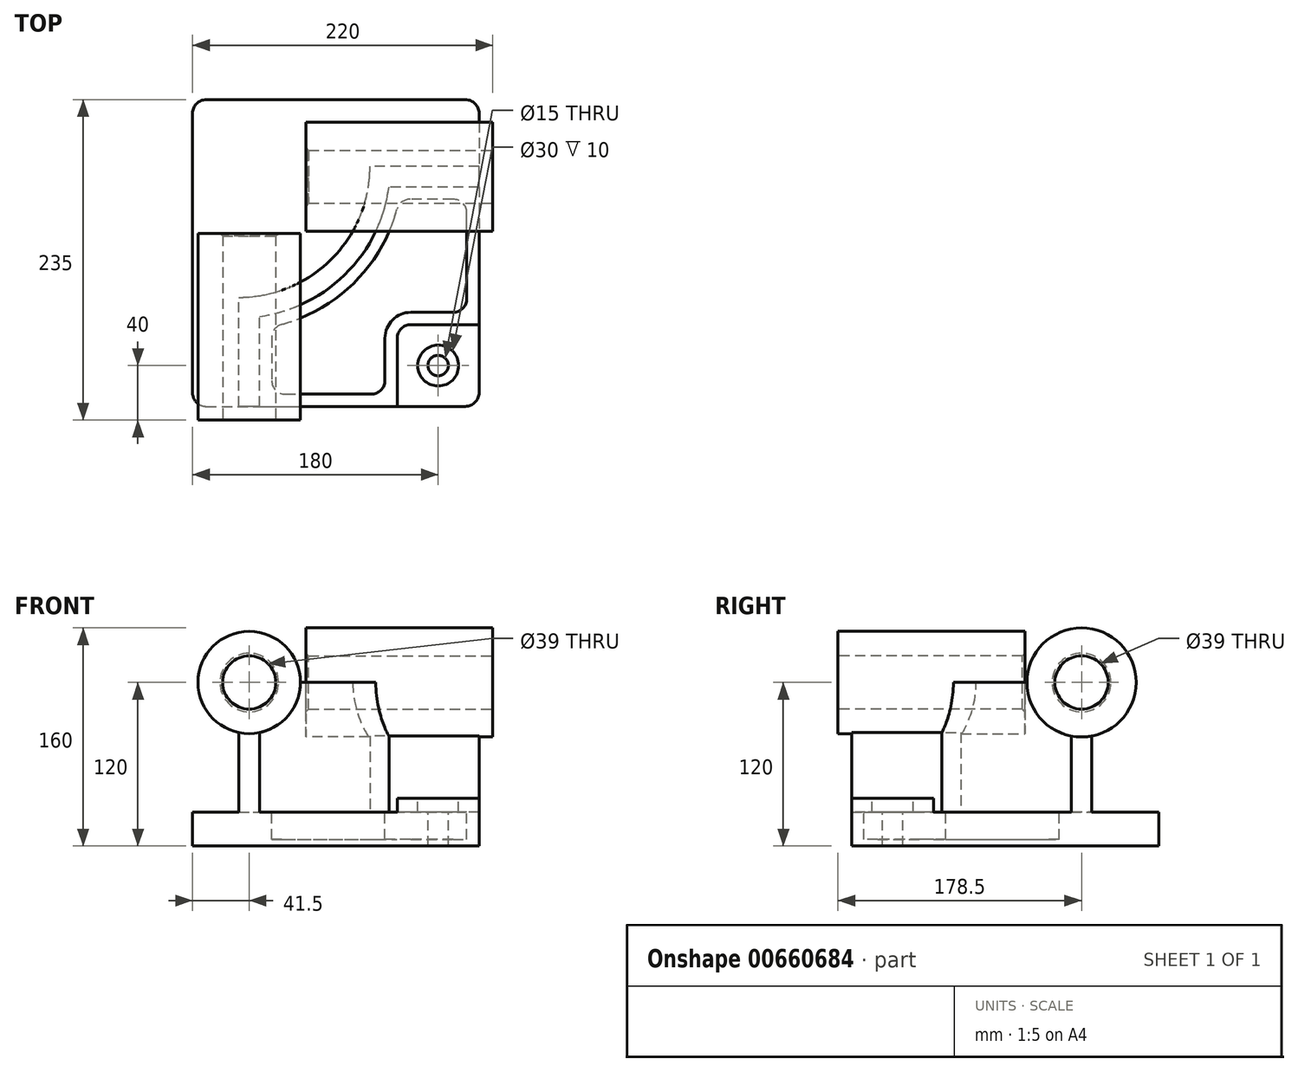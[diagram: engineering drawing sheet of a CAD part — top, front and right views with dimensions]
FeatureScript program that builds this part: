
annotation { "Feature Type Name" : "Feature", "Feature Type Description" : "" }
export const myFeature = defineFeature(function(context is Context, id is Id, definition is map)
    precondition{}
    {
        {
            var Q0;
            Q0=qCreatedBy(makeId("Top.planeOp"),FACE);
            var sketch = newSketch(context, id + "F0", { "sketchPlane" : qUnion([Q0])});
            skLineSegment(sketch, "E0.bottom", {"start": v(-105, 112.5) * mm, "end": v(105, 112.5) * mm});
            skLineSegment(sketch, "E0.top", {"start": v(-105, -112.5) * mm, "end": v(105, -112.5) * mm});
            skLineSegment(sketch, "E0.left", {"start": v(-105, 112.5) * mm, "end": v(-105, -112.5) * mm});
            skLineSegment(sketch, "E0.right", {"start": v(105, 112.5) * mm, "end": v(105, -112.5) * mm});
            skPoint(sketch, "E0.middle", {"position": v(0, 0) * mm});
            skSolve(sketch);
        }
        {
            var Q0;
            Q0=makeQuery(id+"F0.imprint","IMPRINT",FACE,{"disambiguationData":[TD([[makeQuery(id+"F0.imprint","IMPRINT",EDGE,{"derivedFrom":sQuery(id+"F0.wireOp",EDGE,"E0.bottom")}),-1.0]])]});
            extrude(context, id + "F1", {"entities" : qUnion([Q0]), "depth" : 25 * mm, "offsetDistance" : 25.4 * mm});
        }
        {
            var Q0;
            Q0=makeQuery(id+"F1.opExtrude","CAP_FACE",FACE,{"disambiguationData":[OSD([sQuery(id+"F0.wireOp",EDGE,"E0.bottom"),sQuery(id+"F0.wireOp",EDGE,"E0.top"),sQuery(id+"F0.wireOp",EDGE,"E0.left"),sQuery(id+"F0.wireOp",EDGE,"E0.right")])],"isStart":false});
            var sketch = newSketch(context, id + "F2", { "sketchPlane" : qUnion([Q0])});
            skLineSegment(sketch, "E1", {"start": v(-71, -112.5) * mm, "end": v(-71, -32.5) * mm});
            skLineSegment(sketch, "E2", {"start": v(105, 63.5) * mm, "end": v(25, 63.5) * mm});
            skArc(sketch, "E3", {"start": v(-71, -32.5) * mm, "mid": v(-3.12, -4.38) * mm, "end": v(25, 63.5) * mm});
            skLineSegment(sketch, "E4", {"start": v(-71, 63.5) * mm, "end": v(-71, -32.5) * mm, "construction": true});
            skLineSegment(sketch, "E5", {"start": v(-71, 63.5) * mm, "end": v(25, 63.5) * mm, "construction": true});
            skLineSegment(sketch, "E6.0", {"start": v(-56, -112.5) * mm, "end": v(-56, -46.48) * mm});
            skArc(sketch, "E6.1", {"start": v(-56, -46.48) * mm, "mid": v(7.49, -14.99) * mm, "end": v(38.98, 48.5) * mm});
            skLineSegment(sketch, "E6.2", {"start": v(105, 48.5) * mm, "end": v(38.98, 48.5) * mm});
            skLineSegment(sketch, "E7.0", {"start": v(-105, -112.5) * mm, "end": v(105, -112.5) * mm});
            skLineSegment(sketch, "E8.0", {"start": v(105, 112.5) * mm, "end": v(105, -112.5) * mm});
            skSolve(sketch);
        }
        {
            var Q0;
            {var subQ2=sQuery(id+"F2.wireOp",EDGE,"E1");Q0=makeQuery(id+"F2.imprint","IMPRINT",FACE,{"disambiguationData":[TD([[makeQuery(id+"F2.imprint","IMPRINT",EDGE,{"derivedFrom":subQ2}),-1.0]])]});}
            extrude(context, id + "F3", {"entities" : qUnion([Q0]), "operationType" : NewBodyOperationType.ADD, "depth" : 95 * mm, "offsetDistance" : 25.4 * mm});
        }
        {
            var Q0;
            Q0=makeQuery(id+"F3.boolean.opBoolean","MERGE",FACE,{"derivedFrom":[makeQuery(id+"F1.opExtrude","SWEPT_FACE",FACE,{"disambiguationData":[OSD([sQuery(id+"F0.wireOp",EDGE,"E0.top")])]}),makeQuery(id+"F3.opExtrude","SWEPT_FACE",FACE,{"disambiguationData":[OSD([sQuery(id+"F2.wireOp",EDGE,"E7.0")])]})]});
            var sketch = newSketch(context, id + "F4", { "sketchPlane" : qUnion([Q0])});
            skCircle(sketch, "E9", {"center": v(-63.5, 120) * mm, "radius": 37.5 * mm});
            skSolve(sketch);
        }
        {
            var Q0;
            Q0 = qSketchRegion(id + "F4", true);
            extrude(context, id + "F5", {"entities" : qUnion([Q0]), "operationType" : NewBodyOperationType.ADD, "depth" : 10 * mm, "offsetDistance" : 25.4 * mm, "hasSecondDirection" : true, "secondDirectionOppositeDirection" : true, "secondDirectionDepth" : (137 - 10) * mm});
        }
        {
            var Q0;
            Q0=makeQuery(id+"F3.boolean.opBoolean","MERGE",FACE,{"derivedFrom":[makeQuery(id+"F1.opExtrude","SWEPT_FACE",FACE,{"disambiguationData":[OSD([sQuery(id+"F0.wireOp",EDGE,"E0.right")])]}),makeQuery(id+"F3.opExtrude","SWEPT_FACE",FACE,{"disambiguationData":[OSD([sQuery(id+"F2.wireOp",EDGE,"E8.0")])]})]});
            var sketch = newSketch(context, id + "F6", { "sketchPlane" : qUnion([Q0])});
            skCircle(sketch, "E10", {"center": v(56, 120) * mm, "radius": 40 * mm});
            skSolve(sketch);
        }
        {
            var Q0;
            Q0 = qSketchRegion(id + "F6", true);
            extrude(context, id + "F7", {"entities" : qUnion([Q0]), "operationType" : NewBodyOperationType.ADD, "depth" : 10 * mm, "offsetDistance" : 25.4 * mm, "hasSecondDirection" : true, "secondDirectionOppositeDirection" : true, "secondDirectionDepth" : (137 - 10) * mm});
        }
        {
            var Q0;
            {var subQ0=sQuery(id+"F0.wireOp",EDGE,"E0.right");var subQ1=sQuery(id+"F0.wireOp",EDGE,"E0.top");Q0=makeQuery(id+"F3.boolean.opBoolean","SPLIT",FACE,{"disambiguationData":[TD([makeQuery(id+"F3.opExtrude","SWEPT_FACE",FACE,{"disambiguationData":[OSD([sQuery(id+"F2.wireOp",EDGE,"E6.0")])]})])],"derivedFrom":makeQuery(id+"F1.opExtrude","CAP_FACE",FACE,{"disambiguationData":[OSD([sQuery(id+"F0.wireOp",EDGE,"E0.bottom"),subQ1,sQuery(id+"F0.wireOp",EDGE,"E0.left"),subQ0])],"isStart":false})});}
            var sketch = newSketch(context, id + "F8", { "sketchPlane" : qUnion([Q0])});
            skLineSegment(sketch, "E11.bottom", {"start": v(105, -112.5) * mm, "end": v(45, -112.5) * mm});
            skLineSegment(sketch, "E11.top", {"start": v(105, -52.5) * mm, "end": v(45, -52.5) * mm});
            skLineSegment(sketch, "E11.left", {"start": v(105, -112.5) * mm, "end": v(105, -52.5) * mm});
            skLineSegment(sketch, "E11.right", {"start": v(45, -112.5) * mm, "end": v(45, -52.5) * mm});
            skSolve(sketch);
        }
        {
            var Q0;
            Q0 = qSketchRegion(id + "F8", true);
            extrude(context, id + "F9", {"entities" : qUnion([Q0]), "operationType" : NewBodyOperationType.ADD, "depth" : 10 * mm, "offsetDistance" : 25.4 * mm});
        }
        {
            var Q0;
            Q0=makeQuery(id+"F9.opExtrude","SWEPT_EDGE",EDGE,{"disambiguationData":[OSD([sQuery(id+"F8.wireOp",EDGE,"E11.top"),sQuery(id+"F8.wireOp",EDGE,"E11.right")])]});
            fillet(context, id + "F10", {"entities" : qUnion([Q0]), "radius" : 10 * mm, "tangentPropagation" : true, "allowEdgeOverflow" : false});
        }
        {
            var Q0;
            {var subQ0=sQuery(id+"F0.wireOp",EDGE,"E0.right");var subQ1=sQuery(id+"F0.wireOp",EDGE,"E0.top");Q0=makeQuery(id+"F3.boolean.opBoolean","SPLIT",FACE,{"disambiguationData":[TD([makeQuery(id+"F3.opExtrude","SWEPT_FACE",FACE,{"disambiguationData":[OSD([sQuery(id+"F2.wireOp",EDGE,"E6.0")])]})])],"derivedFrom":makeQuery(id+"F1.opExtrude","CAP_FACE",FACE,{"disambiguationData":[OSD([sQuery(id+"F0.wireOp",EDGE,"E0.bottom"),subQ1,sQuery(id+"F0.wireOp",EDGE,"E0.left"),subQ0])],"isStart":false})});}
            var sketch = newSketch(context, id + "F11", { "sketchPlane" : qUnion([Q0])});
            skLineSegment(sketch, "E12.0", {"start": v(-47, -54.08) * mm, "end": v(-47, -103.5) * mm});
            skArc(sketch, "E12.1", {"start": v(46.58, 39.5) * mm, "mid": v(13.85, -21.35) * mm, "end": v(-47, -54.08) * mm});
            skLineSegment(sketch, "E12.2", {"start": v(-47, -103.5) * mm, "end": v(36, -103.5) * mm});
            skLineSegment(sketch, "E12.3", {"start": v(96, 39.5) * mm, "end": v(46.58, 39.5) * mm});
            skLineSegment(sketch, "E12.4", {"start": v(36, -103.5) * mm, "end": v(36, -62.5) * mm});
            skArc(sketch, "E12.5", {"start": v(36, -62.5) * mm, "mid": v(41.56, -49.06) * mm, "end": v(55, -43.5) * mm});
            skLineSegment(sketch, "E12.6", {"start": v(55, -43.5) * mm, "end": v(96, -43.5) * mm});
            skLineSegment(sketch, "E12.7", {"start": v(96, -43.5) * mm, "end": v(96, 39.5) * mm});
            skSolve(sketch);
        }
        {
            var Q0;
            Q0=makeQuery(id+"F11.imprint","IMPRINT",FACE,{"disambiguationData":[TD([[makeQuery(id+"F11.imprint","IMPRINT",EDGE,{"derivedFrom":sQuery(id+"F11.wireOp",EDGE,"E12.0")}),1.0]])]});
            extrude(context, id + "F12", {"entities" : qUnion([Q0]), "operationType" : NewBodyOperationType.REMOVE, "oppositeDirection" : true, "depth" : (25 - 5) * mm, "offsetDistance" : 25.4 * mm});
        }
        {
            var Q0;
            Q0=makeQuery(id+"F9.opExtrude","CAP_FACE",FACE,{"disambiguationData":[OSD([sQuery(id+"F8.wireOp",EDGE,"E11.bottom"),sQuery(id+"F8.wireOp",EDGE,"E11.top"),sQuery(id+"F8.wireOp",EDGE,"E11.left"),sQuery(id+"F8.wireOp",EDGE,"E11.right")])],"isStart":false});
            var sketch = newSketch(context, id + "F13", { "sketchPlane" : qUnion([Q0])});
            skCircle(sketch, "E13", {"center": v(75, -82.5) * mm, "radius": 15 * mm});
            skSolve(sketch);
        }
        {
            var Q0;
            Q0=sQuery(id+"F13.wireOp",VERTEX,"E13.center");
            var Q1;
            Q1=makeQuery(id+"F1.opExtrude","SWEPT_BODY",BODY,{"disambiguationData":[OSD([sQuery(id+"F0.wireOp",EDGE,"E0.bottom"),sQuery(id+"F0.wireOp",EDGE,"E0.top"),sQuery(id+"F0.wireOp",EDGE,"E0.left"),sQuery(id+"F0.wireOp",EDGE,"E0.right")])]});
            hole(context, id + "F14", {"style" : HoleStyle.C_BORE, "endStyle" : HoleEndStyle.THROUGH, "holeDiameter" : 15 * mm, "cBoreDiameter" : 30 * mm, "cBoreDepth" : 10 * mm, "majorDiameter" : 6.35 * mm, "isTappedThrough" : true, "tappedDepth" : 12.7 * mm, "tapClearance" : 3, "locations" : qUnion([Q0]), "scope" : qUnion([Q1])});
        }
        {
            var Q0;
            Q0=makeQuery(id+"F12.boolean.opBoolean","COPY",EDGE,{"derivedFrom":makeQuery(id+"F12.opExtrude","SWEPT_EDGE",EDGE,{"disambiguationData":[OSD([sQuery(id+"F11.wireOp",EDGE,"E12.0"),sQuery(id+"F11.wireOp",EDGE,"E12.1")])]})});
            var Q1;
            Q1=makeQuery(id+"F12.boolean.opBoolean","COPY",EDGE,{"derivedFrom":makeQuery(id+"F12.opExtrude","SWEPT_EDGE",EDGE,{"disambiguationData":[OSD([sQuery(id+"F11.wireOp",EDGE,"E12.1"),sQuery(id+"F11.wireOp",EDGE,"E12.3")])]})});
            var Q2;
            Q2=makeQuery(id+"F12.boolean.opBoolean","COPY",EDGE,{"derivedFrom":makeQuery(id+"F12.opExtrude","SWEPT_EDGE",EDGE,{"disambiguationData":[OSD([sQuery(id+"F11.wireOp",EDGE,"E12.3"),sQuery(id+"F11.wireOp",EDGE,"E12.7")])]})});
            var Q3;
            Q3=makeQuery(id+"F12.boolean.opBoolean","COPY",EDGE,{"derivedFrom":makeQuery(id+"F12.opExtrude","SWEPT_EDGE",EDGE,{"disambiguationData":[OSD([sQuery(id+"F11.wireOp",EDGE,"E12.6"),sQuery(id+"F11.wireOp",EDGE,"E12.7")])]})});
            var Q4;
            Q4=makeQuery(id+"F12.boolean.opBoolean","COPY",EDGE,{"derivedFrom":makeQuery(id+"F12.opExtrude","SWEPT_EDGE",EDGE,{"disambiguationData":[OSD([sQuery(id+"F11.wireOp",EDGE,"E12.2"),sQuery(id+"F11.wireOp",EDGE,"E12.4")])]})});
            var Q5;
            Q5=makeQuery(id+"F12.boolean.opBoolean","COPY",EDGE,{"derivedFrom":makeQuery(id+"F12.opExtrude","SWEPT_EDGE",EDGE,{"disambiguationData":[OSD([sQuery(id+"F11.wireOp",EDGE,"E12.0"),sQuery(id+"F11.wireOp",EDGE,"E12.2")])]})});
            fillet(context, id + "F15", {"entities" : qUnion([Q0, Q1, Q2, Q3, Q4, Q5]), "radius" : 10 * mm, "tangentPropagation" : true, "allowEdgeOverflow" : false});
        }
        {
            var Q0;
            Q0=makeQuery(id+"F5.opExtrude","CAP_FACE",FACE,{"disambiguationData":[OSD([sQuery(id+"F4.wireOp",EDGE,"E9")])],"isStart":false});
            var sketch = newSketch(context, id + "F16", { "sketchPlane" : qUnion([Q0])});
            skCircle(sketch, "E14", {"center": v(-63.5, 120) * mm, "radius": 19.5 * mm});
            skSolve(sketch);
        }
        {
            var Q0;
            Q0 = qSketchRegion(id + "F16", true);
            extrude(context, id + "F17", {"entities" : qUnion([Q0]), "operationType" : NewBodyOperationType.REMOVE, "endBound" : BoundingType.THROUGH_ALL, "oppositeDirection" : true, "depth" : 25.4 * mm, "offsetDistance" : 25.4 * mm});
        }
        {
            var Q0;
            Q0=makeQuery(id+"F7.opExtrude","CAP_FACE",FACE,{"disambiguationData":[OSD([sQuery(id+"F6.wireOp",EDGE,"E10")])],"isStart":false});
            var sketch = newSketch(context, id + "F18", { "sketchPlane" : qUnion([Q0])});
            skCircle(sketch, "E15", {"center": v(56, 120) * mm, "radius": 19.5 * mm});
            skSolve(sketch);
        }
        {
            var Q0;
            Q0=makeQuery(id+"F18.imprint","IMPRINT",FACE,{"disambiguationData":[TD([[makeQuery(id+"F18.imprint","IMPRINT",EDGE,{"derivedFrom":sQuery(id+"F18.wireOp",EDGE,"E15")}),1.0]])]});
            extrude(context, id + "F19", {"entities" : qUnion([Q0]), "operationType" : NewBodyOperationType.REMOVE, "endBound" : BoundingType.THROUGH_ALL, "oppositeDirection" : true, "depth" : 25.4 * mm, "offsetDistance" : 25.4 * mm});
        }
        {
            var Q0;
            Q0=makeQuery(id+"F17.boolean.opBoolean","COPY",EDGE,{"derivedFrom":makeQuery(id+"F17.opExtrude","CAP_EDGE",EDGE,{"disambiguationData":[OSD([sQuery(id+"F16.wireOp",EDGE,"E14")])],"isStart":true})});
            var Q1;
            Q1=makeQuery(id+"F19.boolean.opBoolean","COPY",EDGE,{"derivedFrom":makeQuery(id+"F19.opExtrude","CAP_EDGE",EDGE,{"disambiguationData":[OSD([sQuery(id+"F18.wireOp",EDGE,"E15")])],"isStart":true})});
            var Q2;
            Q2=makeQuery(id+"F19.boolean.opBoolean","INTERSECT",EDGE,{"derivedFrom":[makeQuery(id+"F7.opExtrude","CAP_FACE",FACE,{"disambiguationData":[OSD([sQuery(id+"F6.wireOp",EDGE,"E10")])],"isStart":true}),makeQuery(id+"F19.opExtrude","SWEPT_FACE",FACE,{"disambiguationData":[OSD([sQuery(id+"F18.wireOp",EDGE,"E15")])]})]});
            var Q3;
            Q3=makeQuery(id+"F17.boolean.opBoolean","INTERSECT",EDGE,{"derivedFrom":[makeQuery(id+"F5.opExtrude","CAP_FACE",FACE,{"disambiguationData":[OSD([sQuery(id+"F4.wireOp",EDGE,"E9")])],"isStart":true}),makeQuery(id+"F17.opExtrude","SWEPT_FACE",FACE,{"disambiguationData":[OSD([sQuery(id+"F16.wireOp",EDGE,"E14")])]})]});
            chamfer(context, id + "F20", {"entities" : qUnion([Q0, Q1, Q2, Q3]), "width" : 2 * mm, "tangentPropagation" : true});
        }
        {
            var Q0;
            Q0=makeQuery(id+"F9.boolean.opBoolean","MERGE",EDGE,{"derivedFrom":[makeQuery(id+"F1.opExtrude","SWEPT_EDGE",EDGE,{"disambiguationData":[OSD([sQuery(id+"F0.wireOp",EDGE,"E0.top"),sQuery(id+"F0.wireOp",EDGE,"E0.right")])]}),makeQuery(id+"F9.opExtrude","SWEPT_EDGE",EDGE,{"disambiguationData":[OSD([sQuery(id+"F8.wireOp",EDGE,"E11.bottom"),sQuery(id+"F8.wireOp",EDGE,"E11.left")])]})]});
            var Q1;
            Q1=makeQuery(id+"F1.opExtrude","SWEPT_EDGE",EDGE,{"disambiguationData":[OSD([sQuery(id+"F0.wireOp",EDGE,"E0.top"),sQuery(id+"F0.wireOp",EDGE,"E0.left")])]});
            var Q2;
            Q2=makeQuery(id+"F1.opExtrude","SWEPT_EDGE",EDGE,{"disambiguationData":[OSD([sQuery(id+"F0.wireOp",EDGE,"E0.bottom"),sQuery(id+"F0.wireOp",EDGE,"E0.left")])]});
            var Q3;
            Q3=makeQuery(id+"F1.opExtrude","SWEPT_EDGE",EDGE,{"disambiguationData":[OSD([sQuery(id+"F0.wireOp",EDGE,"E0.bottom"),sQuery(id+"F0.wireOp",EDGE,"E0.right")])]});
            fillet(context, id + "F21", {"entities" : qUnion([Q0, Q1, Q2, Q3]), "radius" : 10 * mm, "tangentPropagation" : true, "allowEdgeOverflow" : false});
        }
    });
